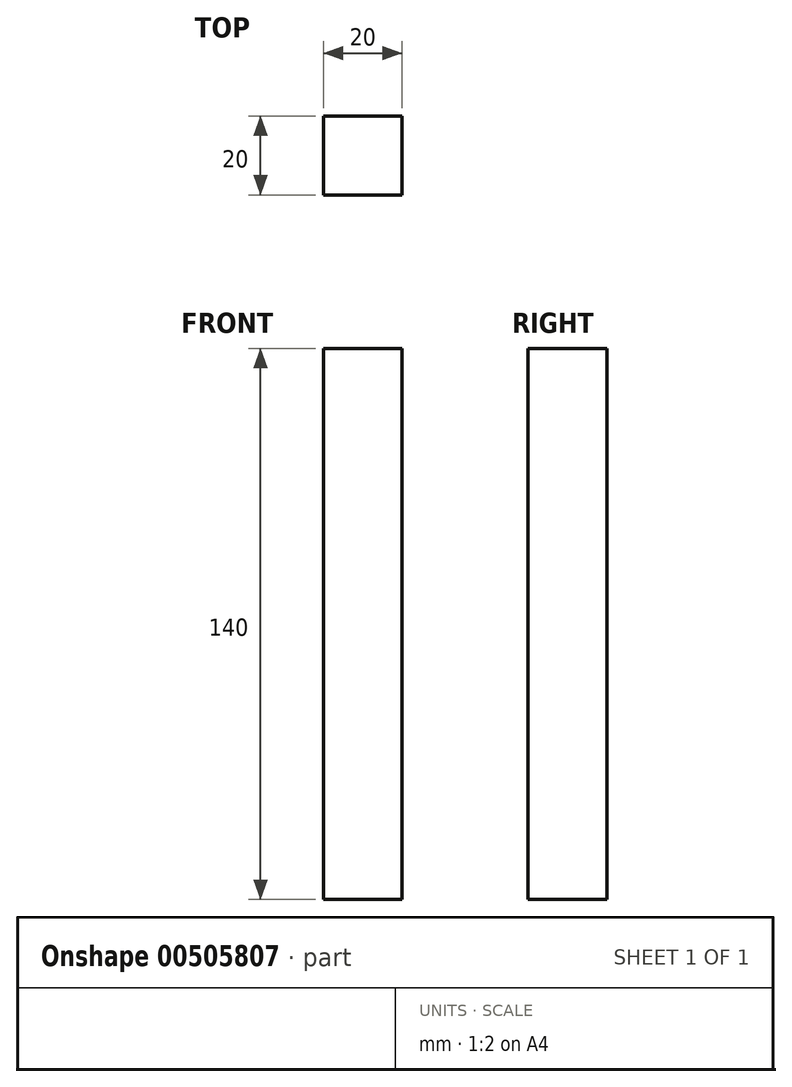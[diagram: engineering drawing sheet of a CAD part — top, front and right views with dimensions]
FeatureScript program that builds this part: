
annotation { "Feature Type Name" : "Feature", "Feature Type Description" : "" }
export const myFeature = defineFeature(function(context is Context, id is Id, definition is map)
    precondition{}
    {
        {
            var Q0;
            Q0=qCreatedBy(makeId("Top.planeOp"),FACE);
            var sketch = newSketch(context, id + "F0", { "sketchPlane" : qUnion([Q0])});
            skLineSegment(sketch, "E0.bottom", {"start": v(10, -10) * mm, "end": v(-10, -10) * mm});
            skLineSegment(sketch, "E0.top", {"start": v(10, 10) * mm, "end": v(-10, 10) * mm});
            skLineSegment(sketch, "E0.left", {"start": v(10, -10) * mm, "end": v(10, 10) * mm});
            skLineSegment(sketch, "E0.right", {"start": v(-10, -10) * mm, "end": v(-10, 10) * mm});
            skPoint(sketch, "E0.middle", {"position": v(0, 0) * mm});
            skSolve(sketch);
        }
        {
            var Q0;
            Q0 = qSketchRegion(id + "F0", true);
            var Q1;
            Q1=sQuery(id+"F0.wireOp",EDGE,"E0.top");
            var Q2;
            Q2=sQuery(id+"F0.wireOp",EDGE,"E0.left");
            var Q3;
            Q3=sQuery(id+"F0.wireOp",EDGE,"E0.bottom");
            var Q4;
            Q4=sQuery(id+"F0.wireOp",EDGE,"E0.right");
            extrude(context, id + "F1", {"entities" : qUnion([Q0]), "bodyType" : ToolBodyType.SURFACE, "surfaceEntities" : qUnion([Q1, Q2, Q3, Q4]), "depth" : 140 * mm});
        }
    });
